# Revit family: Drain_Floor_Round_Zurn-Z415M
name_source: partatom
category: Plumbing Fixtures
units: mm (PartAtom-declared; Revit-internal decimal feet)

## family parameters
Always vertical = Yes
Cut with Voids When Loaded = No
Maintain Annotation Orientation = No
OmniClass Number = 23.70.50.21.24.14
OmniClass Title = Deck Waste Water Drains
Part Type = Normal
Room Calculation Point = No
Round Connector Dimension = Use Radius
Shared = No
Work Plane-Based = No

## types (4) — shared parameters
Approx. Wt. Lbs. = 11.00 lb
Assembly Code = D2030300
CW Connection = No
Default Elevation = 30 "
Description = BODY ASSEMBLY W/ “TYPE M” STRAINER AND “SUR-SET” BUCKET
Grate Radius = 2.519 "
HW Connection = No
Manufacturer = Zurn Water, LLC
Manufacurer Brand = Zurn
Material Main = Iron - Zurn - Cast - Painted - Blue
Modified Date = 12/12/2025
Product Documentation Link = https://files.zurn.com
Product Page URL = https://www.zurn.com
Product data url = https://www.bimobject.com
Strainer Diameter (B) = 5.188 "
Strainer Open Area = 4.5 in²
URL = www.zurn.com
Vent Connection = No
Waste Connection = Yes
zero-valued in all types: CWFU, HWFU, WFU

## per-type parameters (varying)
| type | Body Height (E) | Model | Pipe Size 'A' (Inner Diameter) | Pipe Size 'A' (Inner Radius) | Pipe Size 'A' (Nominal Diameter) | Pipe Size 'A' (Nominal Radius) | Pipe Size 'A' (Outer Diameter) | Pipe Size 'A' (Outer Radius) | Strainer Material | Type Comments |
| ZN415M-4IP | 2.813 " | ZN415M | 4.026 " | 2.013 " | 4 " | 2 " | 4.5 " | 2.25 " | Bronze - Zurn - Polished Nickel | ZN415M with 4 Inch Threaded Outlet |
| ZN415M-3IP | 2.75 " | ZN415M | 3.068 " | 1.534 " | 3 " | 1.5 " | 3.5 " | 1.75 " | Bronze - Zurn - Polished Nickel | ZN415M with 3 Inch Threaded Outlet |
| ZB415M-3IP | 2.75 " | ZB415M | 3.068 " | 1.534 " | 3 " | 1.5 " | 3.5 " | 1.75 " | Bronze - Zurn - Polished | ZB415M with 3 Inch Threaded Outlet |
| ZN415M-2IP | 2.438 " | ZN415M | 2.067 " | 1.034 " | 2 " | 1 " | 2.375 " | 1.188 " | Bronze - Zurn - Polished Nickel | ZN415M with 2 Inch Threaded Outlet |

## geometry (parser evidence)
native form markers: Sweep x2
no freeform markers — native parametric forms only
